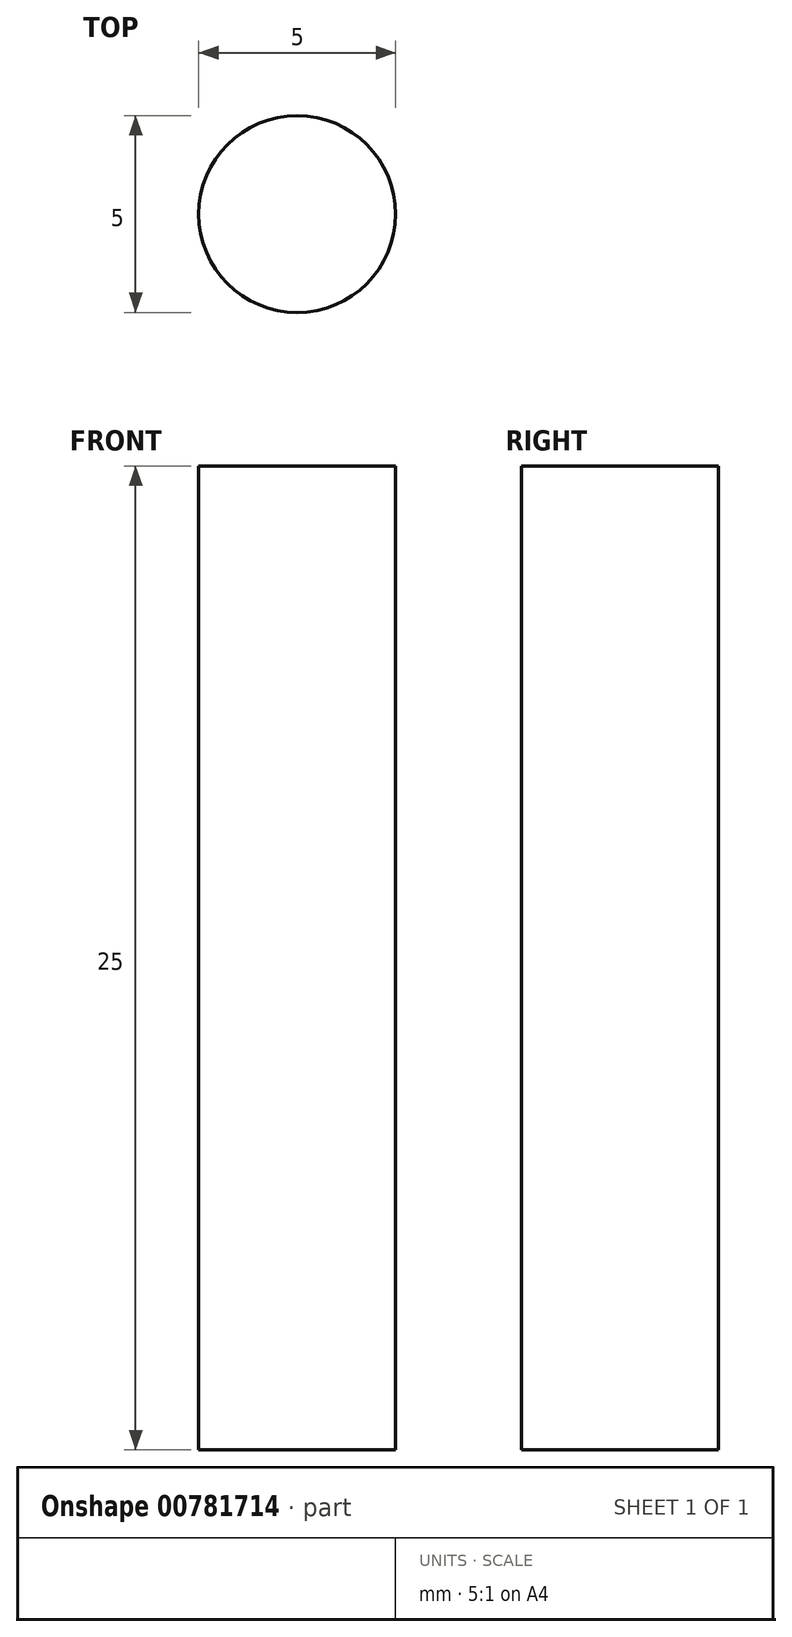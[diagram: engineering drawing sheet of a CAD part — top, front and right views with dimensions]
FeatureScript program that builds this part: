
annotation { "Feature Type Name" : "Feature", "Feature Type Description" : "" }
export const myFeature = defineFeature(function(context is Context, id is Id, definition is map)
    precondition{}
    {
        {
            var Q0;
            Q0=qCreatedBy(makeId("Top.planeOp"),FACE);
            var sketch = newSketch(context, id + "F0", { "sketchPlane" : qUnion([Q0])});
            skCircle(sketch, "E0", {"center": v(0, 0) * mm, "radius": 2.5 * mm});
            skSolve(sketch);
        }
        {
            var Q0;
            Q0=makeQuery(id+"F0.imprint","IMPRINT",FACE,{"disambiguationData":[TD([[makeQuery(id+"F0.imprint","IMPRINT",EDGE,{"derivedFrom":sQuery(id+"F0.wireOp",EDGE,"E0")}),1.0]])]});
            extrude(context, id + "F1", {"entities" : qUnion([Q0]), "depth" : 25 * mm, "offsetDistance" : 25.4 * mm});
        }
    });
